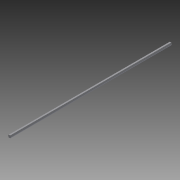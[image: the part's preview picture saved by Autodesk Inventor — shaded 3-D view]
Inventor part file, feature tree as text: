
AUTODESK INVENTOR PART (.ipt)
format: ipt  version: 2014 SP1 (Build 180222100, 222)  size: 70,144 bytes
history: native  units: in
note: dims shown in document units (in); Inventor stores cm internally (conversion verified against a paired STEP export)
features: extrude x1, sketch x1
ambient origin geometry x8: Origin, YZ Plane, XZ Plane, XY Plane, X Axis, Y Axis, Z Axis, Center Point
bodies: Solid1 (feature_tree)
feature tree (2):
  extrude  "Extrusion1"  Depth=0.5in
  sketch  "Sketch1"  dims[d0=0.5in d1=0.5in d2=33.0in d3=0.0in]
